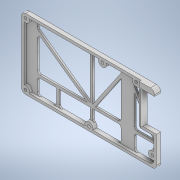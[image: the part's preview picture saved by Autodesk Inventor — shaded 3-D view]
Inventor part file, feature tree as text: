
AUTODESK INVENTOR PART (.ipt)
format: ipt  version: 2021 (Build 250183000, 183)  size: 509,440 bytes
history: native  units: mm
features: sketch x17, extrude x16, fillet x7, hole x1
ambient origin geometry x8: Origin, YZ Plane, XZ Plane, XY Plane, X Axis, Y Axis, Z Axis, Center Point
bodies: Solid1 (feature_tree)
feature tree (41):
  extrude  "Extrusion1"  Depth=52.0mm
  fillet  "Fillet1"  Radius=2.0mm
  extrude  "Extrusion2"  Depth=2.0mm
  hole  "Hole1"  [1 undecoded]
  extrude  "Extrusion3"  Depth=3.0mm
  extrude  "Extrusion4"  Depth=3.0mm
  fillet  "Fillet2"  Radius=50.0mm
  fillet  "Fillet3"  Radius=8.0mm
  extrude  "Extrusion5"  Depth=3.0mm
  extrude  "Extrusion6"  Depth=49.0mm
  extrude  "Extrusion7"  Depth=49.0mm
  extrude  "Extrusion8"  Depth=6.0mm
  extrude  "Extrusion9"  Depth=6.0mm
  fillet  "Fillet5"  Radius=6.0mm
  extrude  "Extrusion10"  Depth=3.0mm TaperAngle=0.0deg
  extrude  "Extrusion11"  Depth=24.0mm
  extrude  "Extrusion12"  Depth=2.0mm
  fillet  "Fillet6"  Radius=15.0mm
  fillet  "Fillet7"  Radius=15.0mm
  extrude  "Extrusion13"  Depth=2.0mm
  extrude  "Extrusion14"  Depth=2.0mm
  extrude  "Extrusion15"  Depth=1.2mm TaperAngle=0.0deg
  extrude  "Extrusion16"  Depth=2.0mm
  fillet  "Fillet8"  Radius=1.2mm
  sketch  "Sketch1"  dims[d0=100.0mm d1=52.0mm d2=2.0mm]
  sketch  "Sketch2"  dims[d3=2.0mm d4=2.0mm]
  sketch  "Sketch3"  dims[d5=2.0mm d6=3.0mm d7=0.0mm]
  sketch  "Sketch4"  dims[d8=3.0mm d9=3.0mm]
  sketch  "Sketch5"  dims[d10=3.0mm d11=3.0mm d12=50.0mm d13=8.0mm]
  sketch  "Sketch6"  dims[d14=97.0mm d15=3.0mm]
  sketch  "Sketch7"  dims[d16=49.0mm d17=60.0mm]
  sketch  "Sketch8"  dims[d18=49.0mm d19=85.0mm]
  sketch  "Sketch9"  dims[d20=49.0mm d21=6.0mm]
  sketch  "Sketch10"  dims[d22=6.0mm d23=6.0mm d24=6.0mm]
  sketch  "Sketch11"  dims[d25=6.0mm d26=3.0mm d27=0.0mm]
  sketch  "Sketch12"  dims[d28=2.0mm d29=6.0mm d30=4.0mm d31=2.0mm d32=90.0deg d33=4.0mm d34=20.594885mm d35=24.0mm]
  sketch  "Sketch13"  dims[d36=2.0mm d37=2.0mm d38=15.0mm d39=15.0mm]
  sketch  "Sketch14"  dims[d40=2.0mm d41=2.0mm]
  sketch  "Sketch15"  dims[d42=2.0mm d43=2.0mm]
  sketch  "Sketch16"  dims[d44=2.0mm d45=1.2mm d46=0.0mm]
  sketch  "Sketch17"  dims[d47=25.0mm d48=2.0mm d49=1.2mm d50=0.0mm d51=2.0mm d52=2.0mm d53=12.0mm d54=29.0mm d55=10.0mm d56=0.0mm d57=2.0mm d58=2.0mm d59=3.0mm d60=0.0mm d62=1.4mm d63=1.4mm d64=3.0mm d65=1.5mm d66=0.0mm d67=3.0mm d68=1.0mm d69=1.0mm d70=3.0mm d71=2.0mm d72=0.0mm d73=3.0mm d74=1.5mm d75=0.0mm d76=3.0mm d77=1.5mm d78=0.0mm d79=10.0mm d80=18.0mm d81=1.0mm d82=1.0mm d83=3.0mm d84=1.2mm d85=0.0mm d86=41.096396mm d87=10.0mm d88=5.0mm d89=5.0mm d90=3.0mm d91=0.8mm d92=4.5mm d93=1.2mm d94=0.0mm d95=2.0mm d96=2.0mm d97=5.0mm d98=0.0mm d99=2.0mm d100=3.0mm d101=0.0mm d102=0.2mm d103=1.5mm d104=0.0mm d105=4.0mm d106=4.5mm d107=0.0mm d108=3.0mm]
note: 1 required parameter value undecoded (feature->parameter linkage not recoverable at this tier; creation-order binding heuristic only, values carry confidence <= 0.55)
